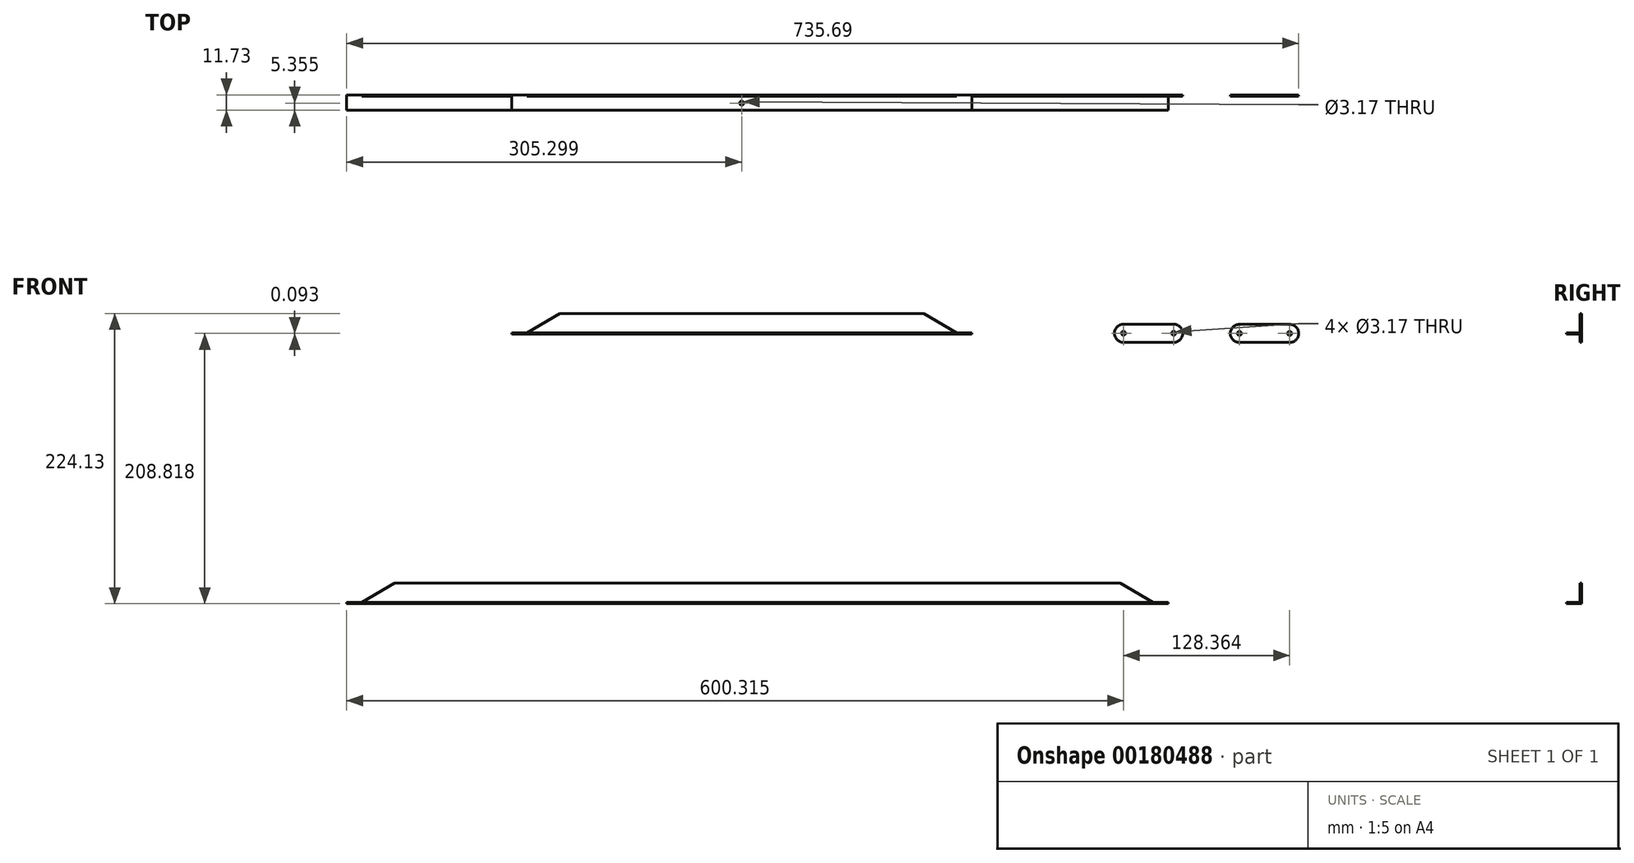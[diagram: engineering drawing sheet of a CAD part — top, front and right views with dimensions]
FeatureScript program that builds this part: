
annotation { "Feature Type Name" : "Feature", "Feature Type Description" : "" }
export const myFeature = defineFeature(function(context is Context, id is Id, definition is map)
    precondition{}
    {
        {
            var Q0;
            Q0=qCreatedBy(makeId("Front.planeOp"),FACE);
            var sketch = newSketch(context, id + "F0", { "sketchPlane" : qUnion([Q0])});
            skLineSegment(sketch, "E0.top", {"start": v(-373.69, -32.4) * mm, "end": v(237.84, -32.4) * mm});
            skLineSegment(sketch, "E1.top", {"start": v(-246.19, 175.85) * mm, "end": v(85.94, 175.85) * mm});
            skLineSegment(sketch, "E2", {"start": v(-220.79, 230.27) * mm, "end": v(-220.79, 114.88) * mm, "construction": true});
            skLineSegment(sketch, "E3", {"start": v(60.54, 221.25) * mm, "end": v(60.54, 127.95) * mm, "construction": true});
            skLineSegment(sketch, "E4", {"start": v(-220.79, 191.73) * mm, "end": v(60.54, 191.73) * mm});
            skLineSegment(sketch, "E5", {"start": v(-348.29, 54.83) * mm, "end": v(-348.29, -100.35) * mm, "construction": true});
            skLineSegment(sketch, "E6", {"start": v(212.44, 24.63) * mm, "end": v(212.44, -95.02) * mm, "construction": true});
            skLineSegment(sketch, "E7", {"start": v(-348.29, -16.52) * mm, "end": v(212.44, -16.52) * mm});
            skLineSegment(sketch, "E8", {"start": v(-246.19, 175.85) * mm, "end": v(-257.92, 175.85) * mm});
            skLineSegment(sketch, "E9", {"start": v(-257.92, 175.85) * mm, "end": v(-257.92, 176.87) * mm});
            skLineSegment(sketch, "E10", {"start": v(-257.92, 176.87) * mm, "end": v(-246.19, 176.87) * mm});
            skLineSegment(sketch, "E11", {"start": v(-246.19, 176.87) * mm, "end": v(-220.79, 191.73) * mm});
            skLineSegment(sketch, "E12", {"start": v(85.94, 175.85) * mm, "end": v(97.68, 175.85) * mm});
            skLineSegment(sketch, "E13", {"start": v(97.68, 175.85) * mm, "end": v(97.68, 176.87) * mm});
            skLineSegment(sketch, "E14", {"start": v(97.68, 176.87) * mm, "end": v(85.94, 176.87) * mm});
            skLineSegment(sketch, "E15", {"start": v(85.94, 176.87) * mm, "end": v(60.54, 191.73) * mm});
            skLineSegment(sketch, "E16", {"start": v(-373.69, -32.4) * mm, "end": v(-385.42, -32.4) * mm});
            skLineSegment(sketch, "E17", {"start": v(-385.42, -32.4) * mm, "end": v(-385.42, -31.38) * mm});
            skLineSegment(sketch, "E18", {"start": v(-385.42, -31.38) * mm, "end": v(-373.69, -31.38) * mm});
            skLineSegment(sketch, "E19", {"start": v(-373.69, -31.38) * mm, "end": v(-348.29, -16.52) * mm});
            skLineSegment(sketch, "E20", {"start": v(237.84, -32.4) * mm, "end": v(249.58, -32.4) * mm});
            skLineSegment(sketch, "E21", {"start": v(249.58, -32.4) * mm, "end": v(249.58, -31.38) * mm});
            skLineSegment(sketch, "E22", {"start": v(249.58, -31.38) * mm, "end": v(237.84, -31.38) * mm});
            skLineSegment(sketch, "E23", {"start": v(237.84, -31.38) * mm, "end": v(212.44, -16.52) * mm});
            skSolve(sketch);
        }
        {
            var Q0;
            Q0=qSketchRegion(id+"F0",true);
            extrude(context, id + "F1", {"entities" : qUnion([Q0]), "depth" : 11.73 * mm});
        }
        {
            var Q0;
            Q0=qCreatedBy(makeId("Front.planeOp"),FACE);
            var sketch = newSketch(context, id + "F2", { "sketchPlane" : qUnion([Q0])});
            skLineSegment(sketch, "E24", {"start": v(214.9, 183.52) * mm, "end": v(253.68, 183.52) * mm});
            skLineSegment(sketch, "E25", {"start": v(214.9, 169.5) * mm, "end": v(253.68, 169.5) * mm});
            skArc(sketch, "E26", {"start": v(214.9, 183.52) * mm, "mid": v(207.89, 176.51) * mm, "end": v(214.9, 169.5) * mm});
            skArc(sketch, "E27", {"start": v(253.68, 169.5) * mm, "mid": v(260.68, 176.51) * mm, "end": v(253.68, 183.52) * mm});
            skLineSegment(sketch, "E28", {"start": v(304.48, 183.42) * mm, "end": v(343.26, 183.42) * mm});
            skLineSegment(sketch, "E29", {"start": v(304.48, 169.41) * mm, "end": v(343.26, 169.41) * mm});
            skArc(sketch, "E30", {"start": v(304.48, 183.42) * mm, "mid": v(297.47, 176.42) * mm, "end": v(304.48, 169.41) * mm});
            skArc(sketch, "E31", {"start": v(343.26, 169.41) * mm, "mid": v(350.27, 176.42) * mm, "end": v(343.26, 183.42) * mm});
            skCircle(sketch, "E32", {"center": v(214.9, 176.51) * mm, "radius": 1.59 * mm});
            skCircle(sketch, "E33", {"center": v(253.68, 176.51) * mm, "radius": 1.59 * mm});
            skCircle(sketch, "E34", {"center": v(304.48, 176.42) * mm, "radius": 1.59 * mm});
            skCircle(sketch, "E35", {"center": v(343.26, 176.42) * mm, "radius": 1.59 * mm});
            skSolve(sketch);
        }
        {
            var Q0;
            Q0=qSketchRegion(id+"F2",true);
            extrude(context, id + "F3", {"entities" : qUnion([Q0]), "depth" : 1.02 * mm});
        }
        {
            var Q0;
            Q0=makeQuery(id+"F1.opExtrude","CAP_FACE",FACE,{"disambiguationData":[OSD([sQuery(id+"F0.wireOp",EDGE,"E0.top"),sQuery(id+"F0.wireOp",EDGE,"E7"),sQuery(id+"F0.wireOp",EDGE,"E16"),sQuery(id+"F0.wireOp",EDGE,"E17"),sQuery(id+"F0.wireOp",EDGE,"E18"),sQuery(id+"F0.wireOp",EDGE,"E19"),sQuery(id+"F0.wireOp",EDGE,"E20"),sQuery(id+"F0.wireOp",EDGE,"E21"),sQuery(id+"F0.wireOp",EDGE,"E22"),sQuery(id+"F0.wireOp",EDGE,"E23")])],"isStart":false});
            var Q1;
            Q1=makeQuery(id+"F1.opExtrude","SWEPT_FACE",FACE,{"disambiguationData":[OSD([sQuery(id+"F0.wireOp",EDGE,"E7")])]});
            var Q2;
            Q2=makeQuery(id+"F1.opExtrude","SWEPT_FACE",FACE,{"disambiguationData":[OSD([sQuery(id+"F0.wireOp",EDGE,"E19")])]});
            var Q3;
            Q3=makeQuery(id+"F1.opExtrude","SWEPT_FACE",FACE,{"disambiguationData":[OSD([sQuery(id+"F0.wireOp",EDGE,"E23")])]});
            shell(context, id + "F4", {"entities" : qUnion([Q0, Q1, Q2, Q3]), "thickness" : 1.02 * mm});
        }
        {
            var Q0;
            Q0=makeQuery(id+"F1.opExtrude","CAP_FACE",FACE,{"disambiguationData":[OSD([sQuery(id+"F0.wireOp",EDGE,"E1.top"),sQuery(id+"F0.wireOp",EDGE,"E4"),sQuery(id+"F0.wireOp",EDGE,"E8"),sQuery(id+"F0.wireOp",EDGE,"E9"),sQuery(id+"F0.wireOp",EDGE,"E10"),sQuery(id+"F0.wireOp",EDGE,"E11"),sQuery(id+"F0.wireOp",EDGE,"E12"),sQuery(id+"F0.wireOp",EDGE,"E13"),sQuery(id+"F0.wireOp",EDGE,"E14"),sQuery(id+"F0.wireOp",EDGE,"E15")])],"isStart":false});
            var Q1;
            Q1=makeQuery(id+"F1.opExtrude","SWEPT_FACE",FACE,{"disambiguationData":[OSD([sQuery(id+"F0.wireOp",EDGE,"E11")])]});
            var Q2;
            Q2=makeQuery(id+"F1.opExtrude","SWEPT_FACE",FACE,{"disambiguationData":[OSD([sQuery(id+"F0.wireOp",EDGE,"E15")])]});
            var Q3;
            Q3=makeQuery(id+"F1.opExtrude","SWEPT_FACE",FACE,{"disambiguationData":[OSD([sQuery(id+"F0.wireOp",EDGE,"E4")])]});
            shell(context, id + "F5", {"entities" : qUnion([Q0, Q1, Q2, Q3]), "thickness" : 1.02 * mm});
        }
        {
            var Q0;
            Q0=qCreatedBy(makeId("Top.planeOp"),FACE);
            var sketch = newSketch(context, id + "F6", { "sketchPlane" : qUnion([Q0])});
            skCircle(sketch, "E36", {"center": v(-80.12, -6.38) * mm, "radius": 1.59 * mm});
            skSolve(sketch);
        }
        {
            var Q0;
            Q0 = qSketchRegion(id + "F6", true);
            extrude(context, id + "F7", {"entities" : qUnion([Q0]), "operationType" : NewBodyOperationType.REMOVE, "depth" : 228.6 * mm});
        }
    });
